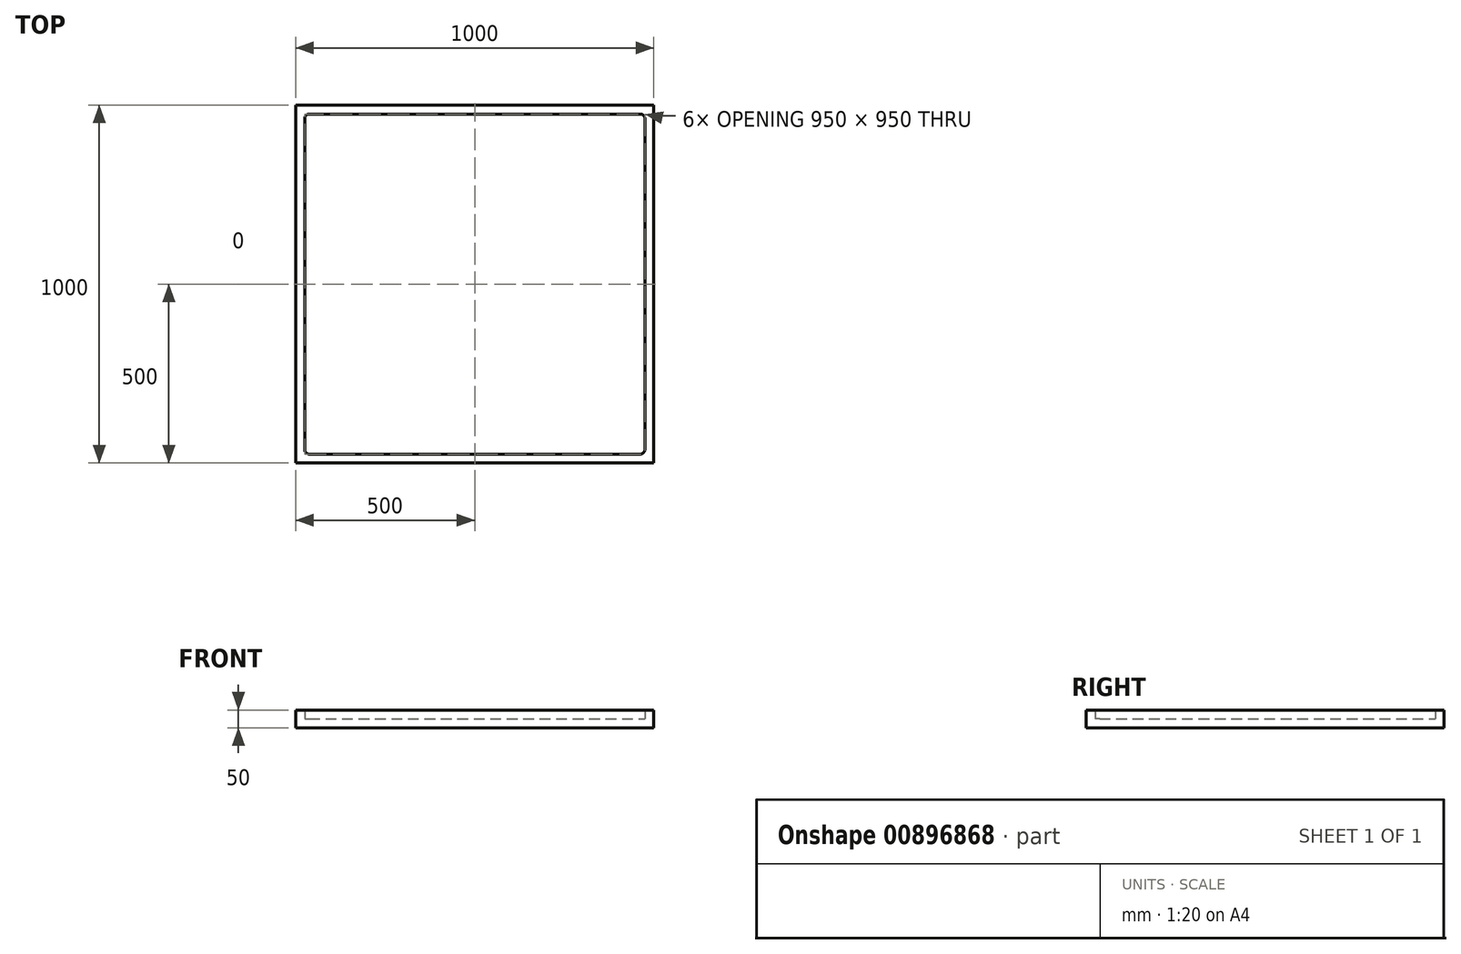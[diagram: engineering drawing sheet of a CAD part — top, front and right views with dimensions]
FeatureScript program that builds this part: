
annotation { "Feature Type Name" : "Feature", "Feature Type Description" : "" }
export const myFeature = defineFeature(function(context is Context, id is Id, definition is map)
    precondition{}
    {
        {
            var Q0;
            Q0=qCreatedBy(makeId("Top.planeOp"),FACE);
            var sketch = newSketch(context, id + "F0", { "sketchPlane" : qUnion([Q0])});
            skLineSegment(sketch, "E0.bottom", {"start": v(0, 0) * mm, "end": v(1000, 0) * mm});
            skLineSegment(sketch, "E0.top", {"start": v(0, 1000) * mm, "end": v(1000, 1000) * mm});
            skLineSegment(sketch, "E0.left", {"start": v(0, 0) * mm, "end": v(0, 1000) * mm});
            skLineSegment(sketch, "E0.right", {"start": v(1000, 0) * mm, "end": v(1000, 1000) * mm});
            skSolve(sketch);
        }
        {
            var Q0;
            Q0=makeQuery(id+"F0.imprint","IMPRINT",FACE,{"disambiguationData":[TD([[makeQuery(id+"F0.imprint","IMPRINT",EDGE,{"derivedFrom":sQuery(id+"F0.wireOp",EDGE,"E0.bottom")}),1.0]])]});
            extrude(context, id + "F1", {"entities" : qUnion([Q0]), "depth" : 50 * mm, "offsetDistance" : 25 * mm});
        }
        {
            var Q0;
            Q0=makeQuery(id+"F1.opExtrude","CAP_FACE",FACE,{"disambiguationData":[OSD([sQuery(id+"F0.wireOp",EDGE,"E0.bottom"),sQuery(id+"F0.wireOp",EDGE,"E0.top"),sQuery(id+"F0.wireOp",EDGE,"E0.left"),sQuery(id+"F0.wireOp",EDGE,"E0.right")])],"isStart":false});
            shell(context, id + "F2", {"entities" : qUnion([Q0]), "thickness" : 25 * mm});
        }
        {
            var Q0;
            Q0=makeQuery(id+"F2.opShell","OFFSET_EDGE",EDGE,{"disambiguationData":[OSD([sQuery(id+"F0.wireOp",EDGE,"E0.top"),sQuery(id+"F0.wireOp",EDGE,"E0.left")])]});
            var Q1;
            Q1=makeQuery(id+"F2.opShell","OFFSET_EDGE",EDGE,{"disambiguationData":[OSD([sQuery(id+"F0.wireOp",EDGE,"E0.top"),sQuery(id+"F0.wireOp",EDGE,"E0.right")])]});
            var Q2;
            Q2=makeQuery(id+"F2.opShell","OFFSET_EDGE",EDGE,{"disambiguationData":[OSD([sQuery(id+"F0.wireOp",EDGE,"E0.bottom"),sQuery(id+"F0.wireOp",EDGE,"E0.right")])]});
            var Q3;
            Q3=makeQuery(id+"F2.opShell","OFFSET_EDGE",EDGE,{"disambiguationData":[OSD([sQuery(id+"F0.wireOp",EDGE,"E0.bottom"),sQuery(id+"F0.wireOp",EDGE,"E0.left")])]});
            fillet(context, id + "F3", {"entities" : qUnion([Q0, Q1, Q2, Q3]), "radius" : 12.5 * mm, "tangentPropagation" : true, "allowEdgeOverflow" : false});
        }
    });
